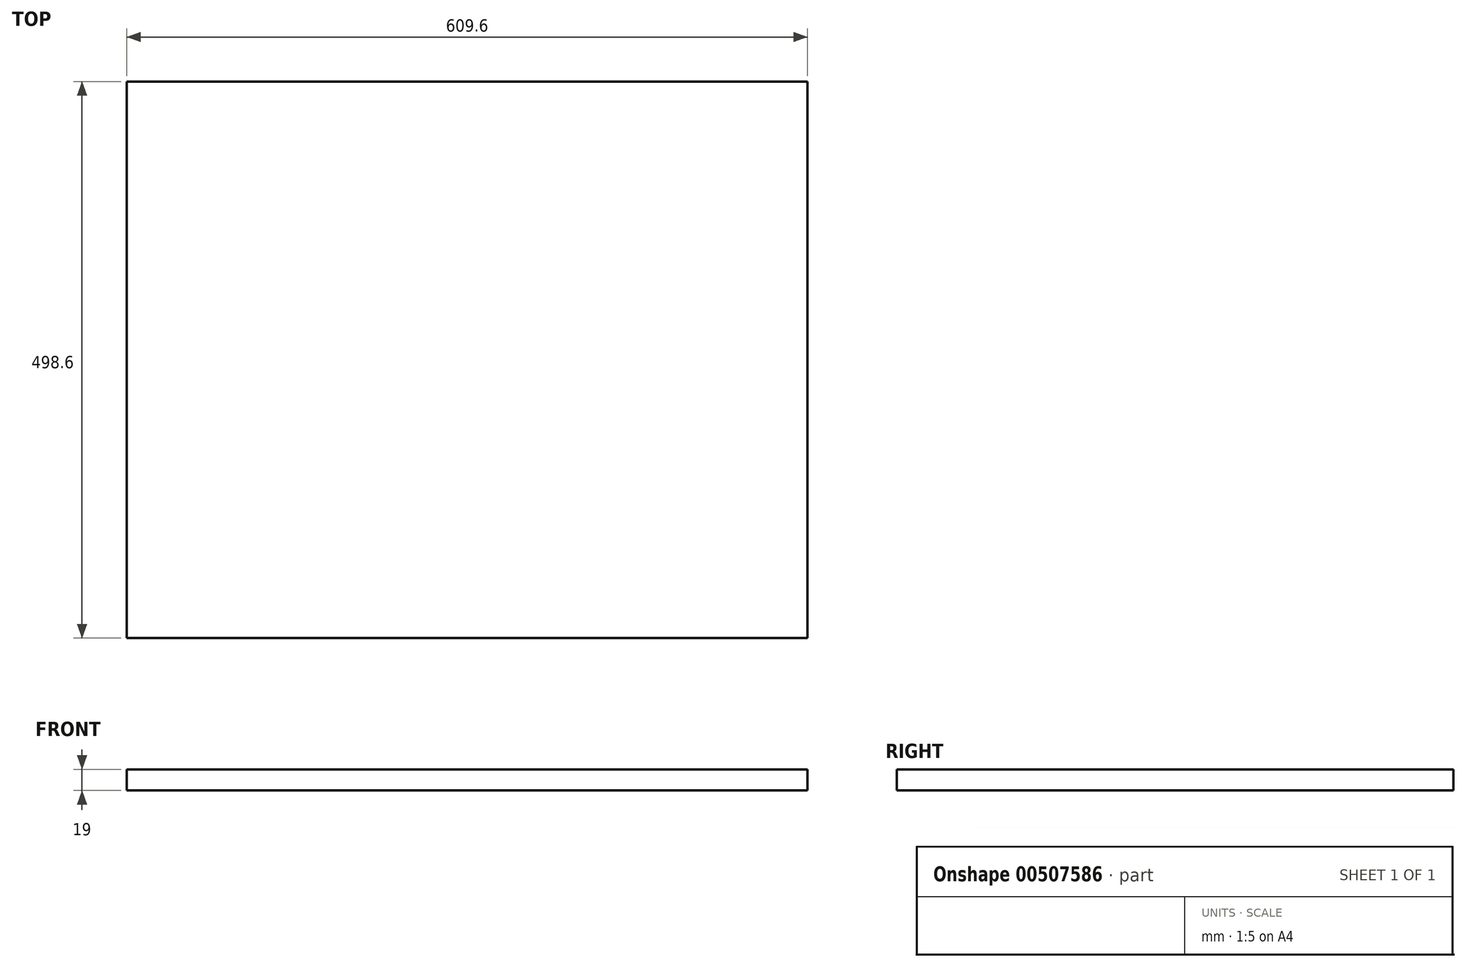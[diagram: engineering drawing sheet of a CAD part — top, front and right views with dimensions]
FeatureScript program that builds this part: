
annotation { "Feature Type Name" : "Feature", "Feature Type Description" : "" }
export const myFeature = defineFeature(function(context is Context, id is Id, definition is map)
    precondition{}
    {
        {
            var Q0;
            Q0=qCreatedBy(makeId("Top.planeOp"),FACE);
            var sketch = newSketch(context, id + "F0", { "sketchPlane" : qUnion([Q0])});
            skLineSegment(sketch, "E0.bottom", {"start": v(-571.1, 442.92) * mm, "end": v(38.5, 442.92) * mm});
            skLineSegment(sketch, "E0.top", {"start": v(-571.1, -55.68) * mm, "end": v(38.5, -55.68) * mm});
            skLineSegment(sketch, "E0.left", {"start": v(-571.1, 442.92) * mm, "end": v(-571.1, -55.68) * mm});
            skLineSegment(sketch, "E0.right", {"start": v(38.5, 442.92) * mm, "end": v(38.5, -55.68) * mm});
            skSolve(sketch);
        }
        {
            var Q0;
            Q0 = qSketchRegion(id + "F0", true);
            extrude(context, id + "F1", {"entities" : qUnion([Q0]), "depth" : 19 * mm});
        }
    });
